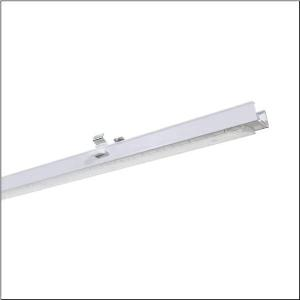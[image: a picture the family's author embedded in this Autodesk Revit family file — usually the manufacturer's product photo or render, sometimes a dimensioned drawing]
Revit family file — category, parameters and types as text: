
# Revit family: trunking_flex_31_51re11ma46b
name_source: partatom
category: Lighting Fixtures
units: mm (PartAtom-declared; Revit-internal decimal feet)

## family parameters
Cut with Voids When Loaded = No
Host = Face
Light Source = No
Part Type = Normal
Room Calculation Point = No
Round Connector Dimension = Use Diameter
Shared = No

## types (1)
- --- (1 x LED, 6400 lm, 40 W, 4000K)
    Apparent Load = 40 VA
    CIE Flux Codes = 83 93 98 100 100
    Color Rendering = 80
    Color Temperature = 4000K
    Default Elevation = 1800 mm
    Description = Trunking Flex 31, luminaire insert, of extruded aluminium section, coated, traffic white (RAL 9016), length: 1.172mm, width: 91mm, height: 53mm, LED rated luminous flux: 6.400lm, light colour: 840, control gear: ON/OFF Multilumen, with system connector: socket, mains connection: 220..240V, AC, 50/60Hz, rated input power: 40W, luminous flux adjustable on luminaire in four steps (3420/4540/5580/6630lm), connected load according to luminous flux setting (20/26/33/40W), primary light control with lens, of plastic, primary optical cover: cover, of PMMA, light emission: direct distribution, protection rating (complete): IP20, insulation class (complete): insulation class I (protective earthing), certification: CE, UKCA, impact resistance: IK02, permissible ambient temperature for indoor applications: -20..+40°C, packaging unit: 1 piece
    Height = 58 mm
    Lamp = 1 x LED
    Lamp Light Flux = 6400 lm
    Lamp Power = 40 W
    Lamp count = 1
    Length = 1172 mm
    Luminous efficacy = 160 lm/W
    Manufacturer = Siteco
    ModVariant = No
    Model = 51RE11MA46B
    Mounting Place = Ceiling
    Mounting Type = Pendant
    Number of Poles = 1
    OnlyDefault = Yes
    Power Factor = 1
    Product Name = Trunking Flex 31
    Product group = luminaire insert
    ProductGroupID = 901
    Protection Class = Protection class I
    Protection Degree = IP 20
    RLX_Detail_Level = 1
    RLX_Emergency_Light_Flux = 0 lm
    RLX_Emergency_Type = 0
    RLX_Emergency_Type_DB = No
    RlxData = <blob elided: 19841 chars, md5=62d072ab>
    Socket = socket
    Standby Power = 0 W
    System Light Flux = 6400 lm
    System Power = 40 W
    Type Comments = factory setting: luminous flux: 100 % | (ON | ON) | 300 mA
    Type Image = l_1266702.jpg
    URL = http://relux.com
    VarID = @adj_018799
    Voltage = 0 V
    Weight = 0.00 kg
    Width = 65 mm

## geometry (parser evidence)
native form markers: Blend x4, Sweep x11
no freeform markers — native parametric forms only
